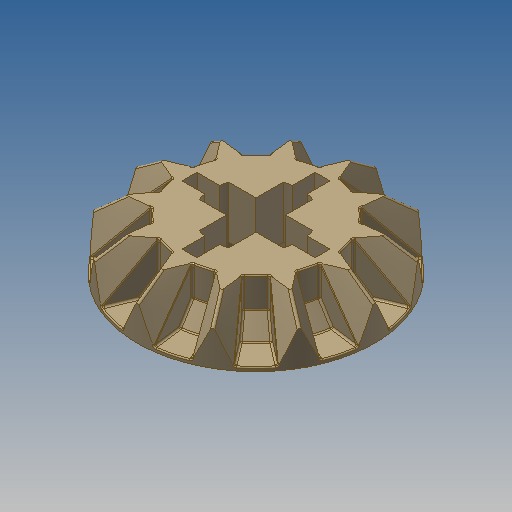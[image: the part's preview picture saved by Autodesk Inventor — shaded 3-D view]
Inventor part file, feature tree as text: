
AUTODESK INVENTOR PART (.ipt)
format: ipt  version: 2022.2 (Build 262287000, 287)  size: 4,789,248 bytes
history: native  units: in
note: dims shown in document units (in); Inventor stores cm internally (conversion verified against a paired STEP export)
features: sketch x9, plane x4, revolve x2, loft x2, fillet x2, other x1, pattern_circular x1, extrude x1, projected_geometry x1
ambient origin geometry x8: Origin, YZ Plane, XZ Plane, XY Plane, X Axis, Y Axis, Z Axis, Center Point
bodies: Solid1 (feature_tree)
feature tree (23):
  sketch  "Sketch2"  dims[d0=0.0472in d1=0.2835in]
  revolve  "Revolution1"  [1 undecoded]
  sketch  "Sketch4"  dims[d4=0.5039in d5=0.1102in]
  sketch  "Sketch6"  dims[d6=0.315in d7=90.0deg d8=0.189in]
  plane  "Work Plane2"
  sketch  "Sketch7"  dims[d9=0.2835in]
  plane  "Work Plane3"
  loft  "Loft1"
  other  "Work Axis1"
  loft  "Loft3"
  revolve  "Revolution2"  Angle=90.0deg
  fillet  "Fillet1"  Radius=0.189in
  pattern_circular  "Circular Pattern1"  [2 undecoded]
  extrude  "Extrusion1"  Depth=0.0039in
  fillet  "Fillet2"  Radius=0.0493in
  sketch  "Sketch3"  dims[d2=0.378in d3=0.0079in]
  sketch  "Sketch8"  dims[d10=0.063in]
  plane  "Work Plane4"
  sketch  "Sketch9"  dims[d11=0.0315in]
  sketch  "Sketch10"  dims[d12=0.3937in d13=0.0in]
  plane  "Work Plane6"
  sketch  "Sketch11"  dims[d14=0.378in d15=0.0394in d16=0.0657in d17=0.0493in d18=0.0206in d19=0.0411in d20=0.0in d21=90.0deg d22=0.0in d23=90.0deg d30=90.0deg d31=0.0472in d32=0.0709in d37=0.0in d38=90.0deg d39=0.0in d40=90.0deg d41=0.0in d42=90.0deg d43=0.0in d44=90.0deg d45=0.0in d46=90.0deg d47=0.0039in d48=4.7244in d49=360.0deg d51=0.0024in d52=0.0039in]
  projected_geometry  "Project Cut Edges1"
note: 3 required parameter values undecoded (feature->parameter linkage not recoverable at this tier; creation-order binding heuristic only, values carry confidence <= 0.55)